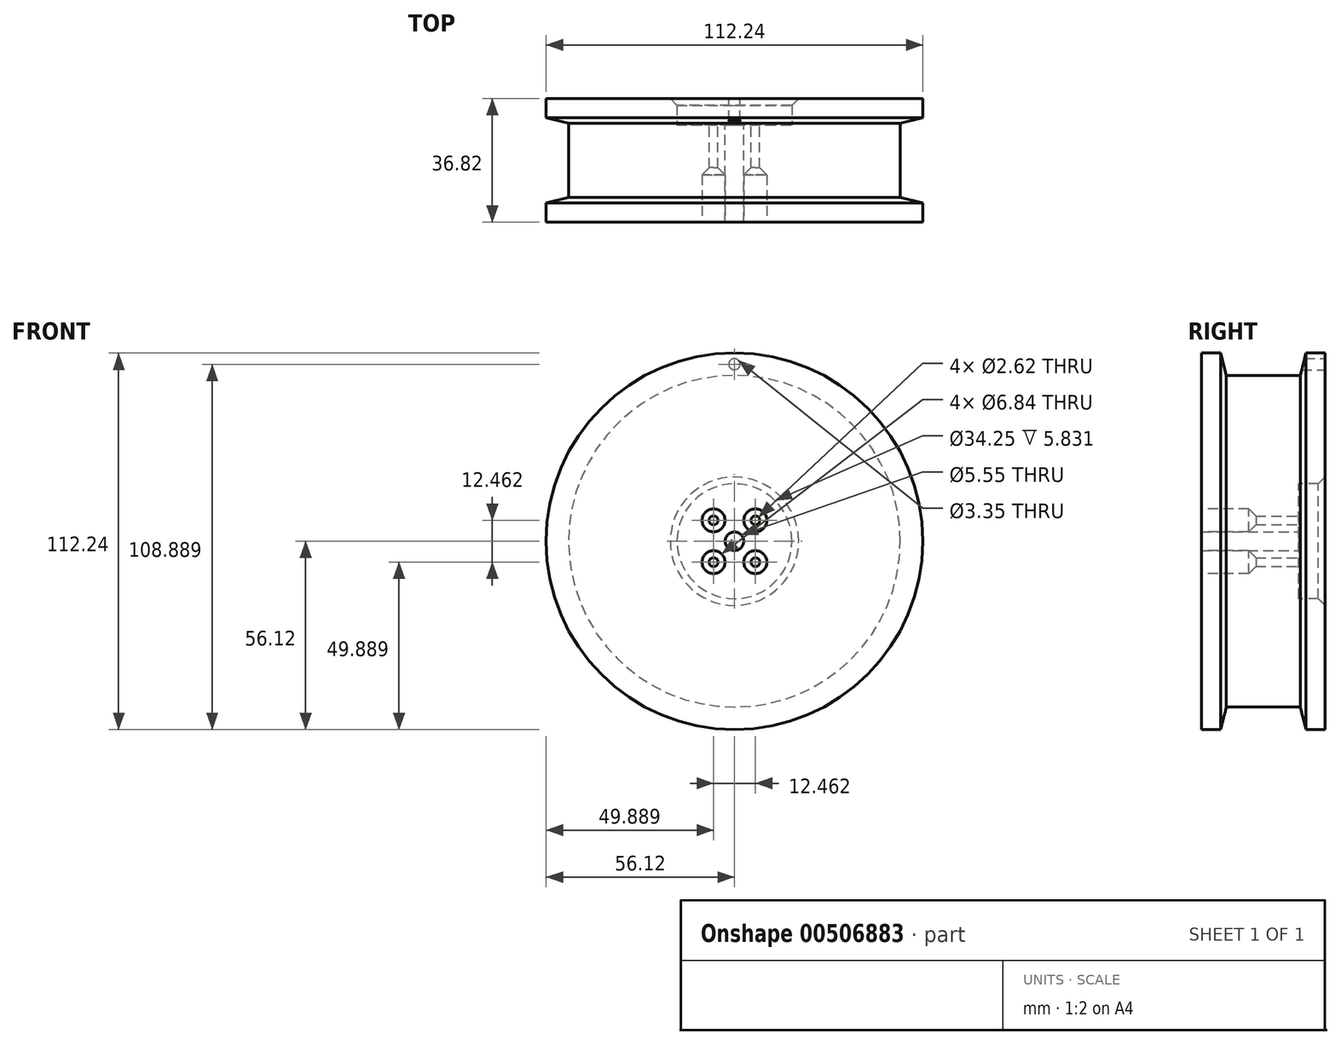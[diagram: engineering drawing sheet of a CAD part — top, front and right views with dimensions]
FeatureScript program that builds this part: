
annotation { "Feature Type Name" : "Feature", "Feature Type Description" : "" }
export const myFeature = defineFeature(function(context is Context, id is Id, definition is map)
    precondition{}
    {
        {
            var Q0;
            Q0=qCreatedBy(makeId("Right.planeOp"),FACE);
            var sketch = newSketch(context, id + "F0", { "sketchPlane" : qUnion([Q0])});
            skLineSegment(sketch, "E0", {"start": v(0, 0) * mm, "end": v(23.9, 0) * mm, "construction": true});
            skLineSegment(sketch, "E1", {"start": v(-18.4, 0) * mm, "end": v(-18.4, 56.12) * mm});
            skLineSegment(sketch, "E2", {"start": v(-18.4, 56.12) * mm, "end": v(-12.73, 56.12) * mm});
            skLineSegment(sketch, "E3", {"start": v(-12.73, 56.12) * mm, "end": v(-11, 49.42) * mm});
            skLineSegment(sketch, "E4", {"start": v(-11, 49.42) * mm, "end": v(0, 49.42) * mm});
            skLineSegment(sketch, "E5", {"start": v(0, 0) * mm, "end": v(0, 37.52) * mm, "construction": true});
            skLineSegment(sketch, "E6.MirrorCS", {"start": v(18.4, 17.12) * mm, "end": v(18.4, 56.12) * mm});
            skLineSegment(sketch, "E7.MirrorCS", {"start": v(18.4, 56.12) * mm, "end": v(12.73, 56.12) * mm});
            skLineSegment(sketch, "E8.MirrorCS", {"start": v(12.73, 56.12) * mm, "end": v(11, 49.42) * mm});
            skLineSegment(sketch, "E9.MirrorCS", {"start": v(11, 49.42) * mm, "end": v(0, 49.42) * mm});
            skLineSegment(sketch, "E10", {"start": v(18.4, 17.12) * mm, "end": v(10.58, 17.12) * mm});
            skLineSegment(sketch, "E11", {"start": v(10.58, 17.12) * mm, "end": v(10.58, 0) * mm});
            skPoint(sketch, "E12.orphan", {"position": v(18.4, 0) * mm});
            skLineSegment(sketch, "E13", {"start": v(-18.4, 0) * mm, "end": v(10.58, 0) * mm});
            skSolve(sketch);
        }
        {
            var Q0;
            Q0 = qSketchRegion(id + "F0", true);
            var Q1;
            Q1=sQuery(id+"F0.wireOp",EDGE,"E0");
            revolve(context, id + "F1", {"entities" : qUnion([Q0]), "axis" : qUnion([Q1]), "revolveType" : RevolveType.FULL});
        }
        {
            var Q0;
            Q0=makeQuery(id+"F1.opRevolve","SWEPT_FACE",FACE,{"disambiguationData":[OSD([sQuery(id+"F0.wireOp",EDGE,"E11")])]});
            var sketch = newSketch(context, id + "F2", { "sketchPlane" : qUnion([Q0])});
            skCircle(sketch, "E14", {"center": v(0, 0) * mm, "radius": 2.78 * mm});
            skCircle(sketch, "E15", {"center": v(-6.23, 6.23) * mm, "radius": 1.31 * mm});
            skLineSegment(sketch, "E16", {"start": v(0, 0) * mm, "end": v(-9.26, 0) * mm, "construction": true});
            skLineSegment(sketch, "E17", {"start": v(0, 0) * mm, "end": v(0, 9.36) * mm, "construction": true});
            skCircle(sketch, "E18.MirrorC", {"center": v(6.23, 6.23) * mm, "radius": 1.31 * mm});
            skCircle(sketch, "E19.MirrorC", {"center": v(6.23, -6.23) * mm, "radius": 1.31 * mm});
            skCircle(sketch, "E20.MirrorC", {"center": v(-6.23, -6.23) * mm, "radius": 1.31 * mm});
            skLineSegment(sketch, "E21", {"start": v(-6.23, 6.23) * mm, "end": v(-6.23, -6.23) * mm, "construction": true});
            skLineSegment(sketch, "E22", {"start": v(6.23, -6.23) * mm, "end": v(-6.23, -6.23) * mm, "construction": true});
            skSolve(sketch);
        }
        {
            var Q0;
            Q0 = qSketchRegion(id + "F2", true);
            extrude(context, id + "F3", {"entities" : qUnion([Q0]), "operationType" : NewBodyOperationType.REMOVE, "endBound" : BoundingType.UP_TO_NEXT, "oppositeDirection" : true, "depth" : 25 * mm});
        }
        {
            var Q0;
            Q0=makeQuery(id+"F1.opRevolve","SWEPT_EDGE",EDGE,{"disambiguationData":[OSD([sQuery(id+"F0.wireOp",EDGE,"E6.MirrorCS"),sQuery(id+"F0.wireOp",EDGE,"E10")])]});
            chamfer(context, id + "F4", {"entities" : qUnion([Q0]), "width" : 2 * mm, "tangentPropagation" : true});
        }
        {
            var Q0;
            Q0=makeQuery(id+"F1.opRevolve","SWEPT_FACE",FACE,{"disambiguationData":[OSD([sQuery(id+"F0.wireOp",EDGE,"E1")])]});
            var sketch = newSketch(context, id + "F5", { "sketchPlane" : qUnion([Q0])});
            skCircle(sketch, "E23", {"center": v(-6.23, 6.23) * mm, "radius": 3.42 * mm});
            skCircle(sketch, "E24", {"center": v(6.23, 6.23) * mm, "radius": 3.42 * mm});
            skCircle(sketch, "E25", {"center": v(6.23, -6.23) * mm, "radius": 3.42 * mm});
            skCircle(sketch, "E26", {"center": v(-6.23, -6.23) * mm, "radius": 3.42 * mm});
            skSolve(sketch);
        }
        {
            var Q0;
            Q0 = qSketchRegion(id + "F5", true);
            extrude(context, id + "F6", {"entities" : qUnion([Q0]), "operationType" : NewBodyOperationType.REMOVE, "oppositeDirection" : true, "depth" : 11.2 * mm});
        }
        {
            var Q0;
            Q0=makeQuery(id+"F6.boolean.opBoolean","INTERSECT",EDGE,{"derivedFrom":[makeQuery(id+"F3.boolean.opBoolean","COPY",FACE,{"derivedFrom":makeQuery(id+"F3.opExtrude","SWEPT_FACE",FACE,{"disambiguationData":[OSD([sQuery(id+"F2.wireOp",EDGE,"E18.MirrorC")])]})}),makeQuery(id+"F6.opExtrude","CAP_FACE",FACE,{"disambiguationData":[OSD([sQuery(id+"F5.wireOp",EDGE,"E23")])],"isStart":false})]});
            var Q1;
            Q1=makeQuery(id+"F6.boolean.opBoolean","INTERSECT",EDGE,{"derivedFrom":[makeQuery(id+"F3.boolean.opBoolean","COPY",FACE,{"derivedFrom":makeQuery(id+"F3.opExtrude","SWEPT_FACE",FACE,{"disambiguationData":[OSD([sQuery(id+"F2.wireOp",EDGE,"E19.MirrorC")])]})}),makeQuery(id+"F6.opExtrude","CAP_FACE",FACE,{"disambiguationData":[OSD([sQuery(id+"F5.wireOp",EDGE,"E26")])],"isStart":false})]});
            var Q2;
            Q2=makeQuery(id+"F6.boolean.opBoolean","INTERSECT",EDGE,{"derivedFrom":[makeQuery(id+"F3.boolean.opBoolean","COPY",FACE,{"derivedFrom":makeQuery(id+"F3.opExtrude","SWEPT_FACE",FACE,{"disambiguationData":[OSD([sQuery(id+"F2.wireOp",EDGE,"E20.MirrorC")])]})}),makeQuery(id+"F6.opExtrude","CAP_FACE",FACE,{"disambiguationData":[OSD([sQuery(id+"F5.wireOp",EDGE,"E25")])],"isStart":false})]});
            var Q3;
            Q3=makeQuery(id+"F6.boolean.opBoolean","INTERSECT",EDGE,{"derivedFrom":[makeQuery(id+"F3.boolean.opBoolean","COPY",FACE,{"derivedFrom":makeQuery(id+"F3.opExtrude","SWEPT_FACE",FACE,{"disambiguationData":[OSD([sQuery(id+"F2.wireOp",EDGE,"E15")])]})}),makeQuery(id+"F6.opExtrude","CAP_FACE",FACE,{"disambiguationData":[OSD([sQuery(id+"F5.wireOp",EDGE,"E24")])],"isStart":false})]});
            chamfer(context, id + "F7", {"entities" : qUnion([Q0, Q1, Q2, Q3]), "width" : 5 * mm, "tangentPropagation" : true});
        }
        {
            var Q0;
            Q0=makeQuery(id+"F1.opRevolve","SWEPT_FACE",FACE,{"disambiguationData":[OSD([sQuery(id+"F0.wireOp",EDGE,"E6.MirrorCS")])]});
            var sketch = newSketch(context, id + "F8", { "sketchPlane" : qUnion([Q0])});
            skCircle(sketch, "E27", {"center": v(0, 52.77) * mm, "radius": 1.68 * mm});
            skCircle(sketch, "E28.0", {"center": v(0, 0) * mm, "radius": 49.42 * mm, "construction": true});
            skLineSegment(sketch, "E29", {"start": v(0, 49.42) * mm, "end": v(0, 56.12) * mm, "construction": true});
            skSolve(sketch);
        }
        {
            var Q0;
            Q0 = qSketchRegion(id + "F8", true);
            extrude(context, id + "F9", {"entities" : qUnion([Q0]), "operationType" : NewBodyOperationType.REMOVE, "endBound" : BoundingType.UP_TO_NEXT, "oppositeDirection" : true, "depth" : 25 * mm});
        }
    });
